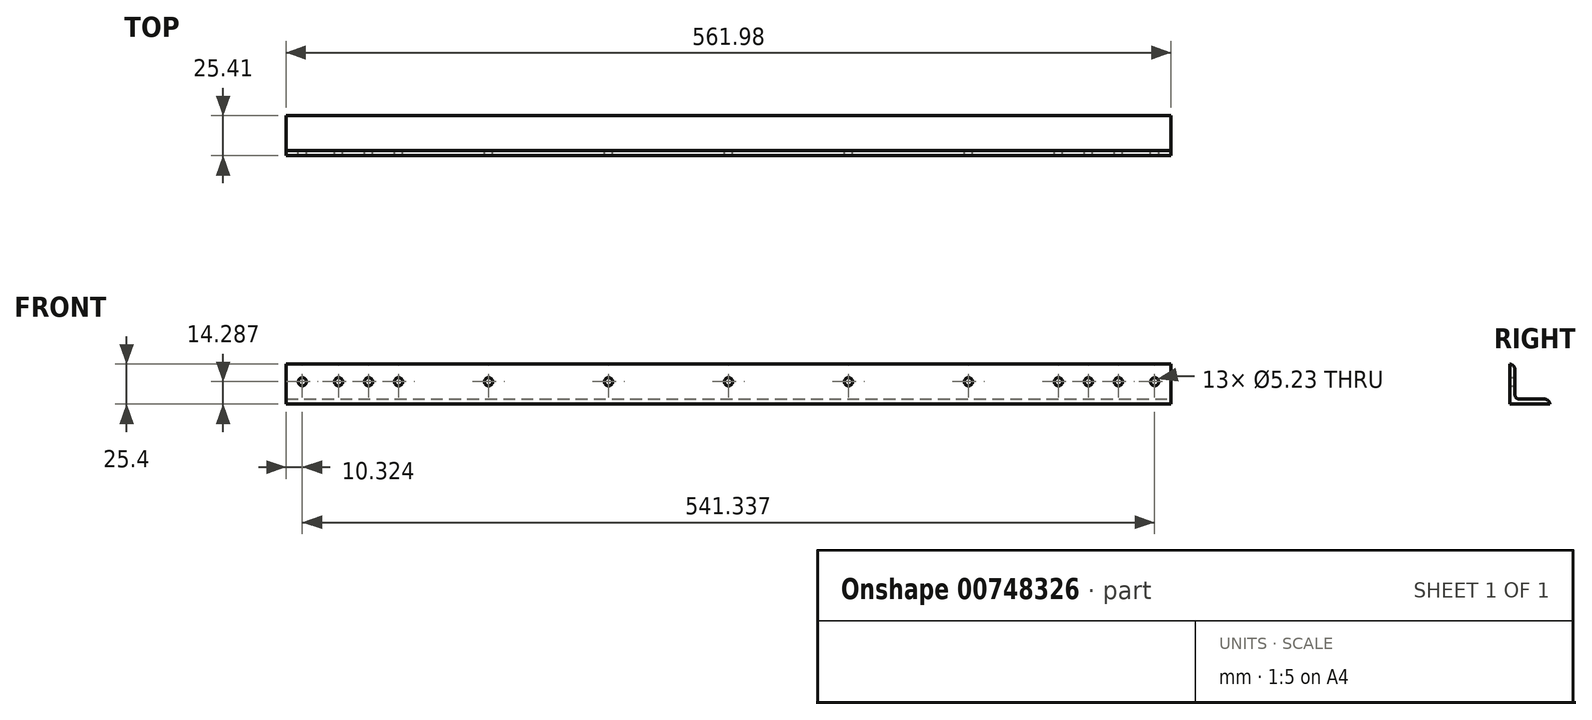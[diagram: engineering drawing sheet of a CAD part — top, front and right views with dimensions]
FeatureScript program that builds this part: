
annotation { "Feature Type Name" : "Feature", "Feature Type Description" : "" }
export const myFeature = defineFeature(function(context is Context, id is Id, definition is map)
    precondition{}
    {
        {
            var Q0;
            Q0=qCreatedBy(makeId("Right.planeOp"),FACE);
            var sketch = newSketch(context, id + "F0", { "sketchPlane" : qUnion([Q0])});
            skLineSegment(sketch, "E0", {"start": v(0, -3.18) * mm, "end": v(0, -19.05) * mm});
            skLineSegment(sketch, "E1", {"start": v(3.18, -22.23) * mm, "end": v(19.05, -22.22) * mm});
            skLineSegment(sketch, "E2.0", {"start": v(-3.17, -25.4) * mm, "end": v(22.23, -25.4) * mm});
            skLineSegment(sketch, "E2.1", {"start": v(-3.17, 0) * mm, "end": v(-3.18, -25.4) * mm});
            skLineSegment(sketch, "E3", {"start": v(-3.18, 0) * mm, "end": v(-3.18, 0) * mm});
            skLineSegment(sketch, "E4", {"start": v(22.23, -25.4) * mm, "end": v(22.23, -25.4) * mm});
            skPoint(sketch, "E5.visualSharp", {"position": v(0, -22.23) * mm});
            skArc(sketch, "E5.filletArc", {"start": v(0, -19.05) * mm, "mid": v(0.93, -21.3) * mm, "end": v(3.18, -22.23) * mm});
            skPoint(sketch, "E6.visualSharp", {"position": v(22.23, -22.22) * mm});
            skArc(sketch, "E6.filletArc", {"start": v(22.23, -25.4) * mm, "mid": v(21.3, -23.15) * mm, "end": v(19.05, -22.22) * mm});
            skPoint(sketch, "E7.visualSharp", {"position": v(0, 0) * mm});
            skArc(sketch, "E7.filletArc", {"start": v(0, -3.18) * mm, "mid": v(-0.93, -0.93) * mm, "end": v(-3.18, 0) * mm});
            skSolve(sketch);
        }
        {
            var Q0;
            Q0=makeQuery(id+"F0.imprint","IMPRINT",FACE,{"disambiguationData":[TD([[makeQuery(id+"F0.imprint","IMPRINT",EDGE,{"derivedFrom":sQuery(id+"F0.wireOp",EDGE,"E0")}),-1.0]])]});
            extrude(context, id + "F1", {"entities" : qUnion([Q0]), "oppositeDirection" : true, "depth" : 561.98 * mm, "offsetDistance" : 25.4 * mm});
        }
        {
            var Q0;
            Q0=makeQuery(id+"F1.opExtrude","SWEPT_FACE",FACE,{"disambiguationData":[OSD([sQuery(id+"F0.wireOp",EDGE,"E0")])]});
            var sketch = newSketch(context, id + "F2", { "sketchPlane" : qUnion([Q0])});
            skCircle(sketch, "E8", {"center": v(10.32, -11.11) * mm, "radius": 2.62 * mm});
            skCircle(sketch, "E9", {"center": v(280.99, -11.11) * mm, "radius": 2.62 * mm});
            skCircle(sketch, "E10", {"center": v(551.66, -11.11) * mm, "radius": 2.62 * mm});
            skCircle(sketch, "E11", {"center": v(128.59, -11.11) * mm, "radius": 2.62 * mm});
            skCircle(sketch, "E12", {"center": v(204.79, -11.11) * mm, "radius": 2.62 * mm});
            skCircle(sketch, "E13", {"center": v(357.19, -11.11) * mm, "radius": 2.62 * mm});
            skCircle(sketch, "E14", {"center": v(433.39, -11.11) * mm, "radius": 2.62 * mm});
            skCircle(sketch, "E15", {"center": v(509.59, -11.11) * mm, "radius": 2.62 * mm});
            skCircle(sketch, "E16", {"center": v(52.39, -11.11) * mm, "radius": 2.62 * mm});
            skCircle(sketch, "E17", {"center": v(33.34, -11.11) * mm, "radius": 2.62 * mm});
            skCircle(sketch, "E18", {"center": v(71.44, -11.11) * mm, "radius": 2.62 * mm});
            skCircle(sketch, "E19", {"center": v(490.54, -11.11) * mm, "radius": 2.62 * mm});
            skCircle(sketch, "E20", {"center": v(528.64, -11.11) * mm, "radius": 2.62 * mm});
            skLineSegment(sketch, "E21", {"start": v(0, -11.11) * mm, "end": v(561.98, -11.11) * mm, "construction": true});
            skLineSegment(sketch, "E22", {"start": v(280.99, -3.18) * mm, "end": v(280.99, -19.05) * mm, "construction": true});
            skLineSegment(sketch, "E23.0", {"start": v(204.79, -3.18) * mm, "end": v(204.79, -12.7) * mm, "construction": true});
            skLineSegment(sketch, "E24.0", {"start": v(128.59, -3.18) * mm, "end": v(128.59, -12.7) * mm, "construction": true});
            skLineSegment(sketch, "E25.0", {"start": v(52.39, -3.18) * mm, "end": v(52.39, -12.7) * mm, "construction": true});
            skLineSegment(sketch, "E26.0", {"start": v(357.19, -3.18) * mm, "end": v(357.19, -12.7) * mm, "construction": true});
            skLineSegment(sketch, "E27.0", {"start": v(433.39, -3.18) * mm, "end": v(433.39, -12.7) * mm, "construction": true});
            skLineSegment(sketch, "E28.0", {"start": v(509.59, -3.18) * mm, "end": v(509.59, -12.7) * mm, "construction": true});
            skSolve(sketch);
        }
        {
            var Q0;
            Q0=qSketchRegion(id+"F2",true);
            extrude(context, id + "F3", {"entities" : qUnion([Q0]), "operationType" : NewBodyOperationType.REMOVE, "oppositeDirection" : true, "depth" : 25.4 * mm, "offsetDistance" : 25.4 * mm});
        }
    });
